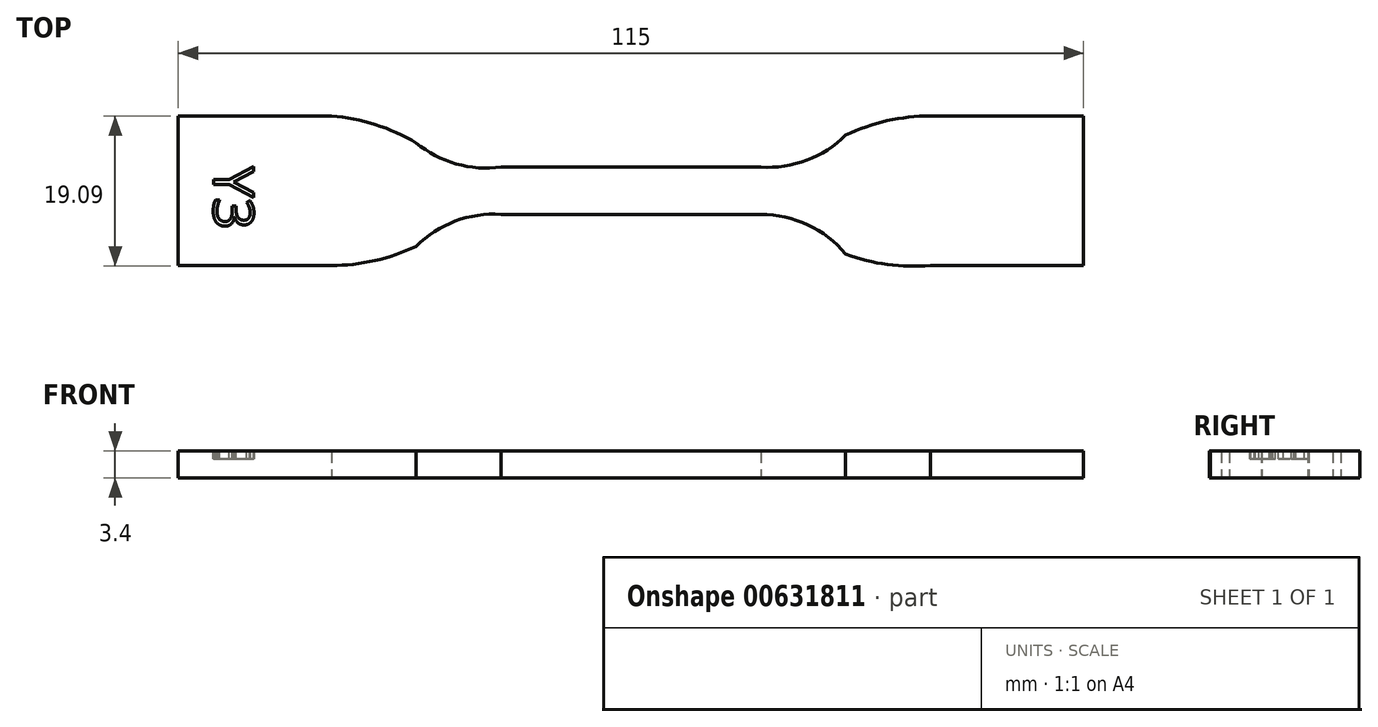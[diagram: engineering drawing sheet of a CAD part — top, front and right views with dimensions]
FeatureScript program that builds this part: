
annotation { "Feature Type Name" : "Feature", "Feature Type Description" : "" }
export const myFeature = defineFeature(function(context is Context, id is Id, definition is map)
    precondition{}
    {
        {
            var Q0;
            Q0=qCreatedBy(makeId("Top.planeOp"),FACE);
            var sketch = newSketch(context, id + "F0", { "sketchPlane" : qUnion([Q0])});
            skLineSegment(sketch, "E0", {"start": v(-33.87, 19.78) * mm, "end": v(-33.87, 0.78) * mm});
            skLineSegment(sketch, "E1", {"start": v(-33.87, 0.78) * mm, "end": v(-14.43, 0.78) * mm});
            skLineSegment(sketch, "E2", {"start": v(-33.87, 19.78) * mm, "end": v(-14.43, 19.78) * mm});
            skLineSegment(sketch, "E3", {"start": v(61.69, 19.78) * mm, "end": v(81.13, 19.78) * mm});
            skLineSegment(sketch, "E4", {"start": v(81.13, 19.78) * mm, "end": v(81.13, 0.78) * mm});
            skLineSegment(sketch, "E5", {"start": v(81.13, 0.78) * mm, "end": v(61.69, 0.78) * mm});
            skLineSegment(sketch, "E6", {"start": v(7.13, 13.28) * mm, "end": v(40.13, 13.28) * mm});
            skLineSegment(sketch, "E7", {"start": v(7.13, 7.28) * mm, "end": v(40.13, 7.28) * mm});
            skArc(sketch, "E8", {"start": v(-3.65, 16.36) * mm, "mid": v(-8.85, 18.69) * mm, "end": v(-14.43, 19.78) * mm});
            skArc(sketch, "E9", {"start": v(-3.65, 16.36) * mm, "mid": v(1.42, 13.7) * mm, "end": v(7.13, 13.28) * mm});
            skArc(sketch, "E10", {"start": v(-14.43, 0.78) * mm, "mid": v(-8.9, 1.4) * mm, "end": v(-3.65, 3.22) * mm});
            skArc(sketch, "E11", {"start": v(7.13, 7.28) * mm, "mid": v(1.3, 6.41) * mm, "end": v(-3.65, 3.22) * mm});
            skArc(sketch, "E12", {"start": v(40.13, 13.28) * mm, "mid": v(45.95, 14.15) * mm, "end": v(50.9, 17.34) * mm});
            skArc(sketch, "E13", {"start": v(61.69, 19.78) * mm, "mid": v(56.16, 19.16) * mm, "end": v(50.9, 17.34) * mm});
            skArc(sketch, "E14", {"start": v(50.9, 2.21) * mm, "mid": v(46.08, 5.95) * mm, "end": v(40.13, 7.28) * mm});
            skArc(sketch, "E15", {"start": v(50.9, 2.21) * mm, "mid": v(56.22, 0.9) * mm, "end": v(61.69, 0.78) * mm});
            skSolve(sketch);
        }
        {
            var Q0;
            Q0=qSketchRegion(id+"F0",true);
            extrude(context, id + "F1", {"entities" : qUnion([Q0]), "depth" : 3.4 * mm, "offsetDistance" : 25 * mm});
        }
        {
            var Q0;
            Q0=makeQuery(id+"F1.opExtrude","CAP_FACE",FACE,{"disambiguationData":[OSD([sQuery(id+"F0.wireOp",EDGE,"E0"),sQuery(id+"F0.wireOp",EDGE,"E1"),sQuery(id+"F0.wireOp",EDGE,"E2"),sQuery(id+"F0.wireOp",EDGE,"E3"),sQuery(id+"F0.wireOp",EDGE,"E4"),sQuery(id+"F0.wireOp",EDGE,"E5"),sQuery(id+"F0.wireOp",EDGE,"E6"),sQuery(id+"F0.wireOp",EDGE,"E7"),sQuery(id+"F0.wireOp",EDGE,"E8"),sQuery(id+"F0.wireOp",EDGE,"E9"),sQuery(id+"F0.wireOp",EDGE,"E10"),sQuery(id+"F0.wireOp",EDGE,"E11"),sQuery(id+"F0.wireOp",EDGE,"E12"),sQuery(id+"F0.wireOp",EDGE,"E13"),sQuery(id+"F0.wireOp",EDGE,"E14"),sQuery(id+"F0.wireOp",EDGE,"E15")])],"isStart":false});
            var sketch = newSketch(context, id + "F2", { "sketchPlane" : qUnion([Q0])});
            skText(sketch, "E16", { "text": "Y3", "fontName": "OpenSans-Regular.ttf"});
            const initialGuessF2  = {"E16": [-0.02937, 0.01335, 0, -1, 0.00508]};
            skSetInitialGuess(sketch, initialGuessF2);
            skSolve(sketch);
        }
        {
            var Q0;
            Q0=qSketchRegion(id+"F2",true);
            extrude(context, id + "F3", {"entities" : qUnion([Q0]), "operationType" : NewBodyOperationType.REMOVE, "oppositeDirection" : true, "depth" : 1 * mm, "offsetDistance" : 25 * mm});
        }
    });
